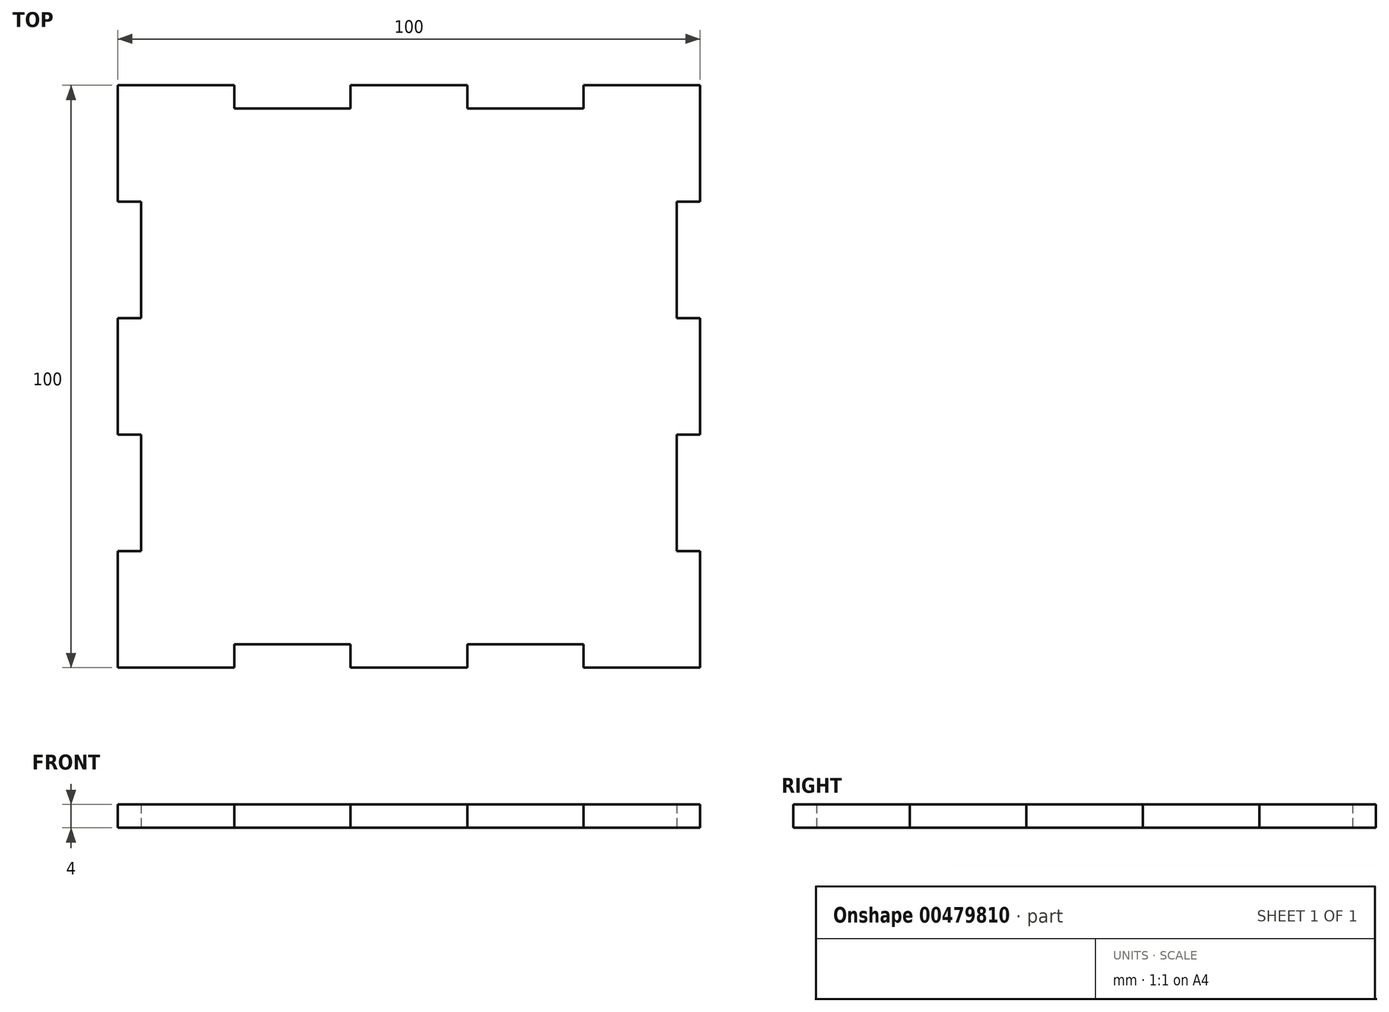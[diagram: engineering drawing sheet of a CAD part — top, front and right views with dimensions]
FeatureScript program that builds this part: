
annotation { "Feature Type Name" : "Feature", "Feature Type Description" : "" }
export const myFeature = defineFeature(function(context is Context, id is Id, definition is map)
    precondition{}
    {
        {
            var Q0;
            Q0=qCreatedBy(makeId("Top.planeOp"),FACE);
            var sketch = newSketch(context, id + "F0", { "sketchPlane" : qUnion([Q0])});
            skLineSegment(sketch, "E0.bottom", {"start": v(0, 0) * mm, "end": v(100, 0) * mm});
            skLineSegment(sketch, "E0.top", {"start": v(0, 100) * mm, "end": v(100, 100) * mm});
            skLineSegment(sketch, "E0.left", {"start": v(0, 0) * mm, "end": v(0, 100) * mm});
            skLineSegment(sketch, "E0.right", {"start": v(100, 0) * mm, "end": v(100, 100) * mm});
            skSolve(sketch);
        }
        {
            var Q0;
            Q0 = qSketchRegion(id + "F0", true);
            extrude(context, id + "F1", {"entities" : qUnion([Q0]), "depth" : 4 * mm});
        }
        {
            var Q0;
            Q0=qCreatedBy(makeId("Top.planeOp"),FACE);
            var sketch = newSketch(context, id + "F2", { "sketchPlane" : qUnion([Q0])});
            skLineSegment(sketch, "E1.bottom", {"start": v(20, 0) * mm, "end": v(40, 0) * mm});
            skLineSegment(sketch, "E1.top", {"start": v(20, 4) * mm, "end": v(40, 4) * mm});
            skLineSegment(sketch, "E1.left", {"start": v(20, 0) * mm, "end": v(20, 4) * mm});
            skLineSegment(sketch, "E1.right", {"start": v(40, 0) * mm, "end": v(40, 4) * mm});
            skLineSegment(sketch, "E2.bottom", {"start": v(60, 0) * mm, "end": v(80, 0) * mm});
            skLineSegment(sketch, "E2.top", {"start": v(60, 4) * mm, "end": v(80, 4) * mm});
            skLineSegment(sketch, "E2.left", {"start": v(60, 0) * mm, "end": v(60, 4) * mm});
            skLineSegment(sketch, "E2.right", {"start": v(80, 0) * mm, "end": v(80, 4) * mm});
            skLineSegment(sketch, "E3.bottom", {"start": v(0, 20) * mm, "end": v(4, 20) * mm});
            skLineSegment(sketch, "E3.top", {"start": v(0, 40) * mm, "end": v(4, 40) * mm});
            skLineSegment(sketch, "E3.left", {"start": v(0, 20) * mm, "end": v(0, 40) * mm});
            skLineSegment(sketch, "E3.right", {"start": v(4, 20) * mm, "end": v(4, 40) * mm});
            skLineSegment(sketch, "E4.bottom", {"start": v(0, 60) * mm, "end": v(4, 60) * mm});
            skLineSegment(sketch, "E4.top", {"start": v(0, 80) * mm, "end": v(4, 80) * mm});
            skLineSegment(sketch, "E4.left", {"start": v(0, 60) * mm, "end": v(0, 80) * mm});
            skLineSegment(sketch, "E4.right", {"start": v(4, 60) * mm, "end": v(4, 80) * mm});
            skLineSegment(sketch, "E5.bottom", {"start": v(20, 100) * mm, "end": v(40, 100) * mm});
            skLineSegment(sketch, "E5.top", {"start": v(20, 96) * mm, "end": v(40, 96) * mm});
            skLineSegment(sketch, "E5.left", {"start": v(20, 100) * mm, "end": v(20, 96) * mm});
            skLineSegment(sketch, "E5.right", {"start": v(40, 100) * mm, "end": v(40, 96) * mm});
            skLineSegment(sketch, "E6.bottom", {"start": v(60, 96) * mm, "end": v(80, 96) * mm});
            skLineSegment(sketch, "E6.top", {"start": v(60, 100) * mm, "end": v(80, 100) * mm});
            skLineSegment(sketch, "E6.left", {"start": v(60, 96) * mm, "end": v(60, 100) * mm});
            skLineSegment(sketch, "E6.right", {"start": v(80, 96) * mm, "end": v(80, 100) * mm});
            skLineSegment(sketch, "E7.bottom", {"start": v(96, 80) * mm, "end": v(100, 80) * mm});
            skLineSegment(sketch, "E7.top", {"start": v(96, 60) * mm, "end": v(100, 60) * mm});
            skLineSegment(sketch, "E7.left", {"start": v(96, 80) * mm, "end": v(96, 60) * mm});
            skLineSegment(sketch, "E7.right", {"start": v(100, 80) * mm, "end": v(100, 60) * mm});
            skLineSegment(sketch, "E8.bottom", {"start": v(100, 20) * mm, "end": v(96, 20) * mm});
            skLineSegment(sketch, "E8.top", {"start": v(100, 40) * mm, "end": v(96, 40) * mm});
            skLineSegment(sketch, "E8.left", {"start": v(100, 20) * mm, "end": v(100, 40) * mm});
            skLineSegment(sketch, "E8.right", {"start": v(96, 20) * mm, "end": v(96, 40) * mm});
            skSolve(sketch);
        }
        {
            var Q0;
            Q0 = qSketchRegion(id + "F2", true);
            extrude(context, id + "F3", {"entities" : qUnion([Q0]), "operationType" : NewBodyOperationType.REMOVE, "depth" : 4 * mm});
        }
    });
